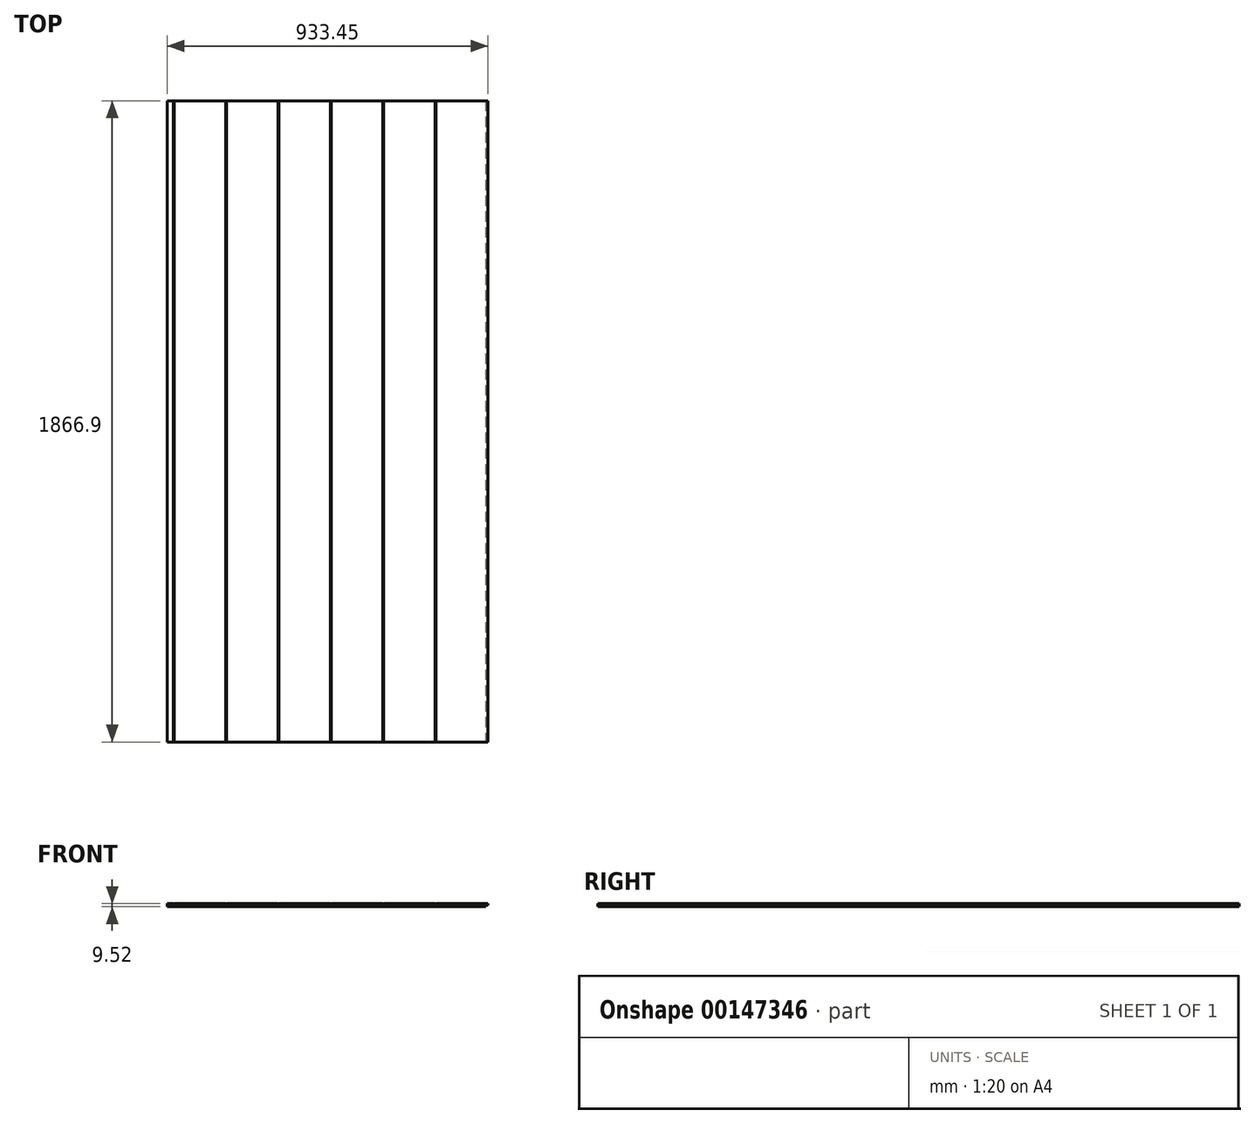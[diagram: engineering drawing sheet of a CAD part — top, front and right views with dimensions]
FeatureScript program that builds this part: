
annotation { "Feature Type Name" : "Feature", "Feature Type Description" : "" }
export const myFeature = defineFeature(function(context is Context, id is Id, definition is map)
    precondition{}
    {
        {
            var Q0;
            Q0=qCreatedBy(makeId("Top.planeOp"),FACE);
            var sketch = newSketch(context, id + "F0", { "sketchPlane" : qUnion([Q0])});
            skLineSegment(sketch, "E0.bottom", {"start": v(-609.6, 1911.45) * mm, "end": v(609.6, 1911.45) * mm});
            skLineSegment(sketch, "E0.top", {"start": v(-609.6, -523.78) * mm, "end": v(609.6, -523.78) * mm});
            skLineSegment(sketch, "E0.left", {"start": v(-609.6, 1911.45) * mm, "end": v(-609.6, -523.78) * mm});
            skLineSegment(sketch, "E0.right", {"start": v(609.6, 1911.45) * mm, "end": v(609.6, -523.78) * mm});
            skSolve(sketch);
        }
        {
            var Q0;
            Q0=qSketchRegion(id+"F0",true);
            extrude(context, id + "F1", {"entities" : qUnion([Q0]), "endBound" : BoundingType.SYMMETRIC, "depth" : 9.52 * mm});
        }
        {
            var Q0;
            Q0=makeQuery(id+"F1.opExtrude","SWEPT_FACE",FACE,{"disambiguationData":[OSD([sQuery(id+"F0.wireOp",EDGE,"E0.top")])]});
            var sketch = newSketch(context, id + "F2", { "sketchPlane" : qUnion([Q0])});
            skLineSegment(sketch, "E1", {"start": v(609.6, 0) * mm, "end": v(603.25, 0) * mm});
            skPoint(sketch, "E1.endSnap0", {"position": v(609.6, 0) * mm});
            skLineSegment(sketch, "E2", {"start": v(603.25, 0) * mm, "end": v(603.25, -4.76) * mm});
            skLineSegment(sketch, "E3", {"start": v(609.6, 0) * mm, "end": v(609.6, -4.76) * mm});
            skLineSegment(sketch, "E4", {"start": v(609.6, -4.76) * mm, "end": v(603.25, -4.76) * mm});
            skLineSegment(sketch, "E5.bottom", {"start": v(-609.6, 4.76) * mm, "end": v(-603.25, 4.76) * mm});
            skLineSegment(sketch, "E5.top", {"start": v(-609.6, 0) * mm, "end": v(-603.25, 0) * mm});
            skLineSegment(sketch, "E5.left", {"start": v(-609.6, 4.76) * mm, "end": v(-609.6, 0) * mm});
            skLineSegment(sketch, "E5.right", {"start": v(-603.25, 4.76) * mm, "end": v(-603.25, 0) * mm});
            skSolve(sketch);
        }
        {
            var Q0;
            Q0=qSketchRegion(id+"F2",true);
            extrude(context, id + "F3", {"entities" : qUnion([Q0]), "operationType" : NewBodyOperationType.REMOVE, "endBound" : BoundingType.THROUGH_ALL, "oppositeDirection" : true, "depth" : 25.4 * mm});
        }
        {
            var Q0;
            Q0=makeQuery(id+"F1.opExtrude","SWEPT_FACE",FACE,{"disambiguationData":[OSD([sQuery(id+"F0.wireOp",EDGE,"E0.top")])]});
            var sketch = newSketch(context, id + "F4", { "sketchPlane" : qUnion([Q0])});
            skLineSegment(sketch, "E6.bottom", {"start": v(-458, 4.76) * mm, "end": v(-456.4, 4.76) * mm});
            skLineSegment(sketch, "E6.top", {"start": v(-458, 3.17) * mm, "end": v(-456.4, 3.17) * mm});
            skLineSegment(sketch, "E6.left", {"start": v(-458, 4.76) * mm, "end": v(-458, 3.17) * mm});
            skLineSegment(sketch, "E6.right", {"start": v(-456.4, 4.76) * mm, "end": v(-456.4, 3.17) * mm});
            skPoint(sketch, "E7", {"position": v(-457.2, 3.17) * mm});
            skPoint(sketch, "E8.1.0.0", {"position": v(-304.8, 3.17) * mm});
            skLineSegment(sketch, "E8.1.0.1", {"start": v(-305.6, 4.76) * mm, "end": v(-304, 4.76) * mm});
            skLineSegment(sketch, "E8.1.0.2", {"start": v(-305.6, 3.17) * mm, "end": v(-304, 3.17) * mm});
            skLineSegment(sketch, "E8.1.0.3", {"start": v(-305.6, 4.76) * mm, "end": v(-305.6, 3.17) * mm});
            skLineSegment(sketch, "E8.1.0.4", {"start": v(-304, 4.76) * mm, "end": v(-304, 3.17) * mm});
            skPoint(sketch, "E8.2.0.0", {"position": v(-152.4, 3.17) * mm});
            skLineSegment(sketch, "E8.2.0.1", {"start": v(-153.2, 4.76) * mm, "end": v(-151.6, 4.76) * mm});
            skLineSegment(sketch, "E8.2.0.2", {"start": v(-153.2, 3.17) * mm, "end": v(-151.6, 3.17) * mm});
            skLineSegment(sketch, "E8.2.0.3", {"start": v(-153.2, 4.76) * mm, "end": v(-153.2, 3.17) * mm});
            skLineSegment(sketch, "E8.2.0.4", {"start": v(-151.6, 4.76) * mm, "end": v(-151.6, 3.17) * mm});
            skPoint(sketch, "E8.3.0.0", {"position": v(0, 3.17) * mm});
            skLineSegment(sketch, "E8.3.0.1", {"start": v(-0.8, 4.76) * mm, "end": v(0.8, 4.76) * mm});
            skLineSegment(sketch, "E8.3.0.2", {"start": v(-0.8, 3.17) * mm, "end": v(0.8, 3.17) * mm});
            skLineSegment(sketch, "E8.3.0.3", {"start": v(-0.8, 4.76) * mm, "end": v(-0.8, 3.17) * mm});
            skLineSegment(sketch, "E8.3.0.4", {"start": v(0.8, 4.76) * mm, "end": v(0.8, 3.17) * mm});
            skPoint(sketch, "E8.4.0.0", {"position": v(152.4, 3.17) * mm});
            skLineSegment(sketch, "E8.4.0.1", {"start": v(151.6, 4.76) * mm, "end": v(153.2, 4.76) * mm});
            skLineSegment(sketch, "E8.4.0.2", {"start": v(151.6, 3.17) * mm, "end": v(153.2, 3.17) * mm});
            skLineSegment(sketch, "E8.4.0.3", {"start": v(151.6, 4.76) * mm, "end": v(151.6, 3.17) * mm});
            skLineSegment(sketch, "E8.4.0.4", {"start": v(153.2, 4.76) * mm, "end": v(153.2, 3.17) * mm});
            skPoint(sketch, "E8.5.0.0", {"position": v(304.8, 3.17) * mm});
            skLineSegment(sketch, "E8.5.0.1", {"start": v(304, 4.76) * mm, "end": v(305.6, 4.76) * mm});
            skLineSegment(sketch, "E8.5.0.2", {"start": v(304, 3.17) * mm, "end": v(305.6, 3.17) * mm});
            skLineSegment(sketch, "E8.5.0.3", {"start": v(304, 4.76) * mm, "end": v(304, 3.17) * mm});
            skLineSegment(sketch, "E8.5.0.4", {"start": v(305.6, 4.76) * mm, "end": v(305.6, 3.17) * mm});
            skPoint(sketch, "E8.6.0.0", {"position": v(457.2, 3.17) * mm});
            skLineSegment(sketch, "E8.6.0.1", {"start": v(456.4, 4.76) * mm, "end": v(458, 4.76) * mm});
            skLineSegment(sketch, "E8.6.0.2", {"start": v(456.4, 3.17) * mm, "end": v(458, 3.17) * mm});
            skLineSegment(sketch, "E8.6.0.3", {"start": v(456.4, 4.76) * mm, "end": v(456.4, 3.17) * mm});
            skLineSegment(sketch, "E8.6.0.4", {"start": v(458, 4.76) * mm, "end": v(458, 3.17) * mm});
            skLineSegment(sketch, "E8.direction1", {"start": v(-457.2, 3.17) * mm, "end": v(-304.8, 3.17) * mm, "construction": true});
            skSolve(sketch);
        }
        {
            var Q0;
            Q0=qSketchRegion(id+"F4",true);
            extrude(context, id + "F5", {"entities" : qUnion([Q0]), "operationType" : NewBodyOperationType.REMOVE, "endBound" : BoundingType.THROUGH_ALL, "oppositeDirection" : true, "depth" : 25.4 * mm});
        }
        {
            var Q0;
            Q0=makeQuery(id+"F1.opExtrude","SWEPT_FACE",FACE,{"disambiguationData":[OSD([sQuery(id+"F0.wireOp",EDGE,"E0.top")])]});
            var sketch = newSketch(context, id + "F6", { "sketchPlane" : qUnion([Q0])});
            skLineSegment(sketch, "E9", {"start": v(-0.8, 3.17) * mm, "end": v(0, 3.17) * mm});
            skLineSegment(sketch, "E10.bottom", {"start": v(-609.6, -4.76) * mm, "end": v(-323.85, -4.76) * mm});
            skLineSegment(sketch, "E10.top", {"start": v(-609.6, 4.76) * mm, "end": v(-323.85, 4.76) * mm});
            skLineSegment(sketch, "E10.left", {"start": v(-609.6, -4.76) * mm, "end": v(-609.6, 4.76) * mm});
            skLineSegment(sketch, "E10.right", {"start": v(-323.85, -4.76) * mm, "end": v(-323.85, 4.76) * mm});
            skSolve(sketch);
        }
        {
            var Q0;
            Q0=qSketchRegion(id+"F6",true);
            extrude(context, id + "F7", {"entities" : qUnion([Q0]), "operationType" : NewBodyOperationType.REMOVE, "endBound" : BoundingType.THROUGH_ALL, "oppositeDirection" : true, "depth" : 25.4 * mm});
        }
        {
            var Q0;
            Q0=makeQuery(id+"F7.boolean.opBoolean","COPY",FACE,{"derivedFrom":makeQuery(id+"F7.opExtrude","SWEPT_FACE",FACE,{"disambiguationData":[OSD([sQuery(id+"F6.wireOp",EDGE,"E10.right")])]})});
            var sketch = newSketch(context, id + "F8", { "sketchPlane" : qUnion([Q0])});
            skLineSegment(sketch, "E11.bottom", {"start": v(-1911.45, -4.76) * mm, "end": v(-1343.12, -4.76) * mm});
            skLineSegment(sketch, "E11.top", {"start": v(-1911.45, 4.76) * mm, "end": v(-1343.12, 4.76) * mm});
            skLineSegment(sketch, "E11.left", {"start": v(-1911.45, -4.76) * mm, "end": v(-1911.45, 4.76) * mm});
            skLineSegment(sketch, "E11.right", {"start": v(-1343.12, -4.76) * mm, "end": v(-1343.12, 4.76) * mm});
            skSolve(sketch);
        }
        {
            var Q0;
            Q0=qSketchRegion(id+"F8",true);
            extrude(context, id + "F9", {"entities" : qUnion([Q0]), "operationType" : NewBodyOperationType.REMOVE, "endBound" : BoundingType.THROUGH_ALL, "oppositeDirection" : true, "depth" : 25.4 * mm});
        }
    });
